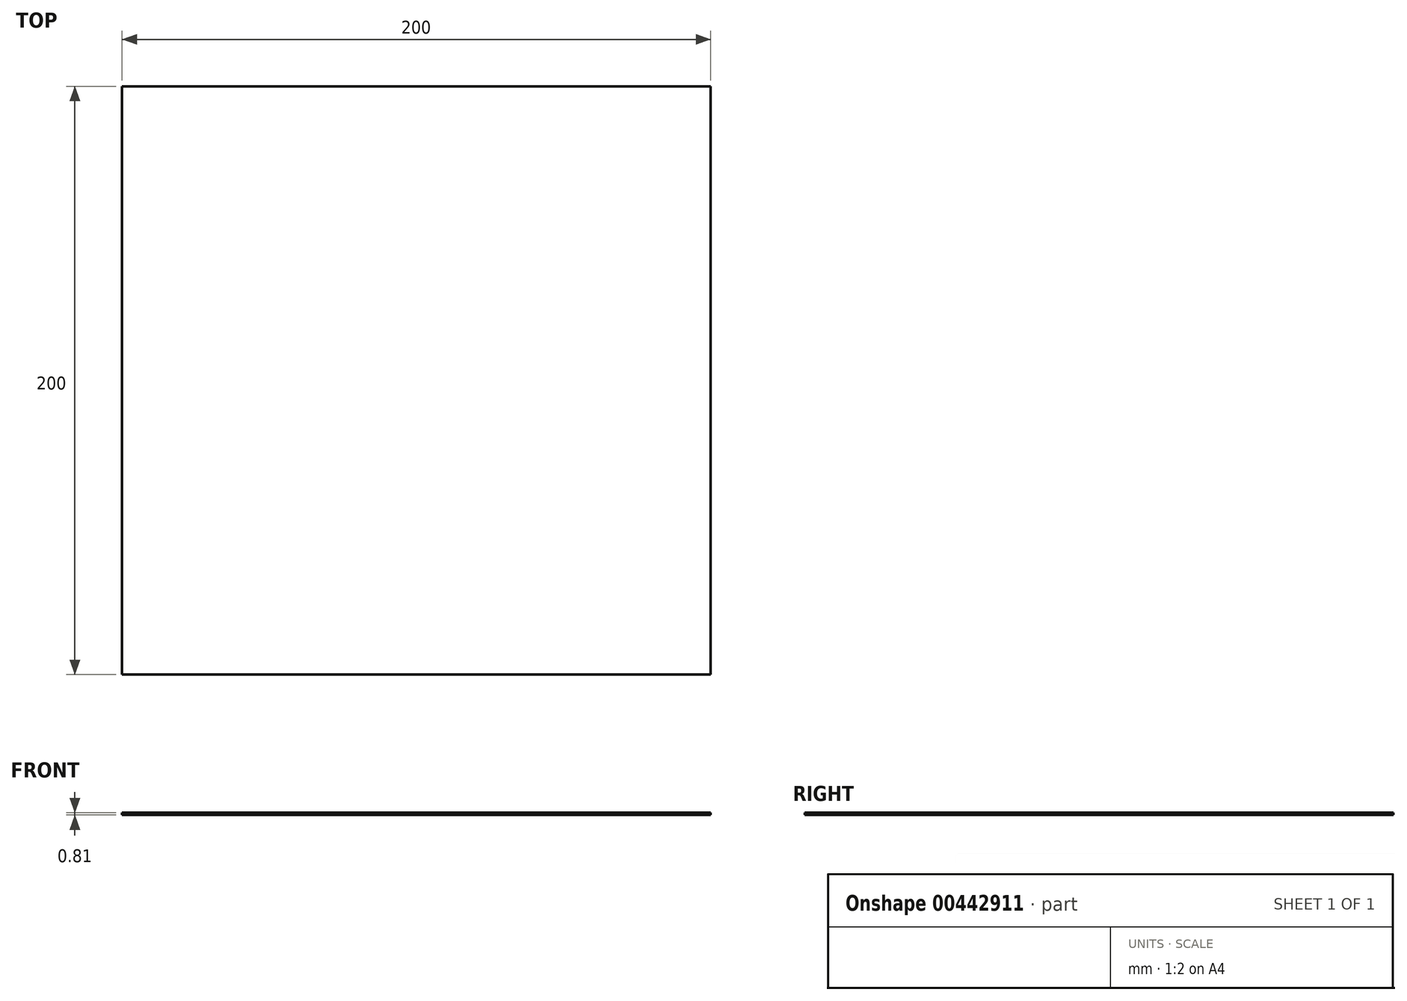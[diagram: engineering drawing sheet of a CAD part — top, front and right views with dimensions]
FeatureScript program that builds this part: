
annotation { "Feature Type Name" : "Feature", "Feature Type Description" : "" }
export const myFeature = defineFeature(function(context is Context, id is Id, definition is map)
    precondition{}
    {
        {
            var Q0;
            Q0=qCreatedBy(makeId("Top.planeOp"),FACE);
            var sketch = newSketch(context, id + "F0", { "sketchPlane" : qUnion([Q0])});
            skLineSegment(sketch, "E0.bottom", {"start": v(-100, 99.7) * mm, "end": v(100, 99.7) * mm});
            skLineSegment(sketch, "E0.top", {"start": v(-100, -100.3) * mm, "end": v(100, -100.3) * mm});
            skLineSegment(sketch, "E0.left", {"start": v(-100, 99.7) * mm, "end": v(-100, -100.3) * mm});
            skLineSegment(sketch, "E0.right", {"start": v(100, 99.7) * mm, "end": v(100, -100.3) * mm});
            skPoint(sketch, "E1", {"position": v(0, 99.7) * mm});
            skPoint(sketch, "E2", {"position": v(100, 0) * mm});
            skSolve(sketch);
        }
        {
            var Q0;
            Q0=makeQuery(id+"F0.imprint","IMPRINT",FACE,{"disambiguationData":[TD([[makeQuery(id+"F0.imprint","IMPRINT",EDGE,{"derivedFrom":sQuery(id+"F0.wireOp",EDGE,"E0.bottom")}),-1.0]])]});
            extrude(context, id + "F1", {"entities" : qUnion([Q0]), "depth" : 0.81 * mm});
        }
    });
